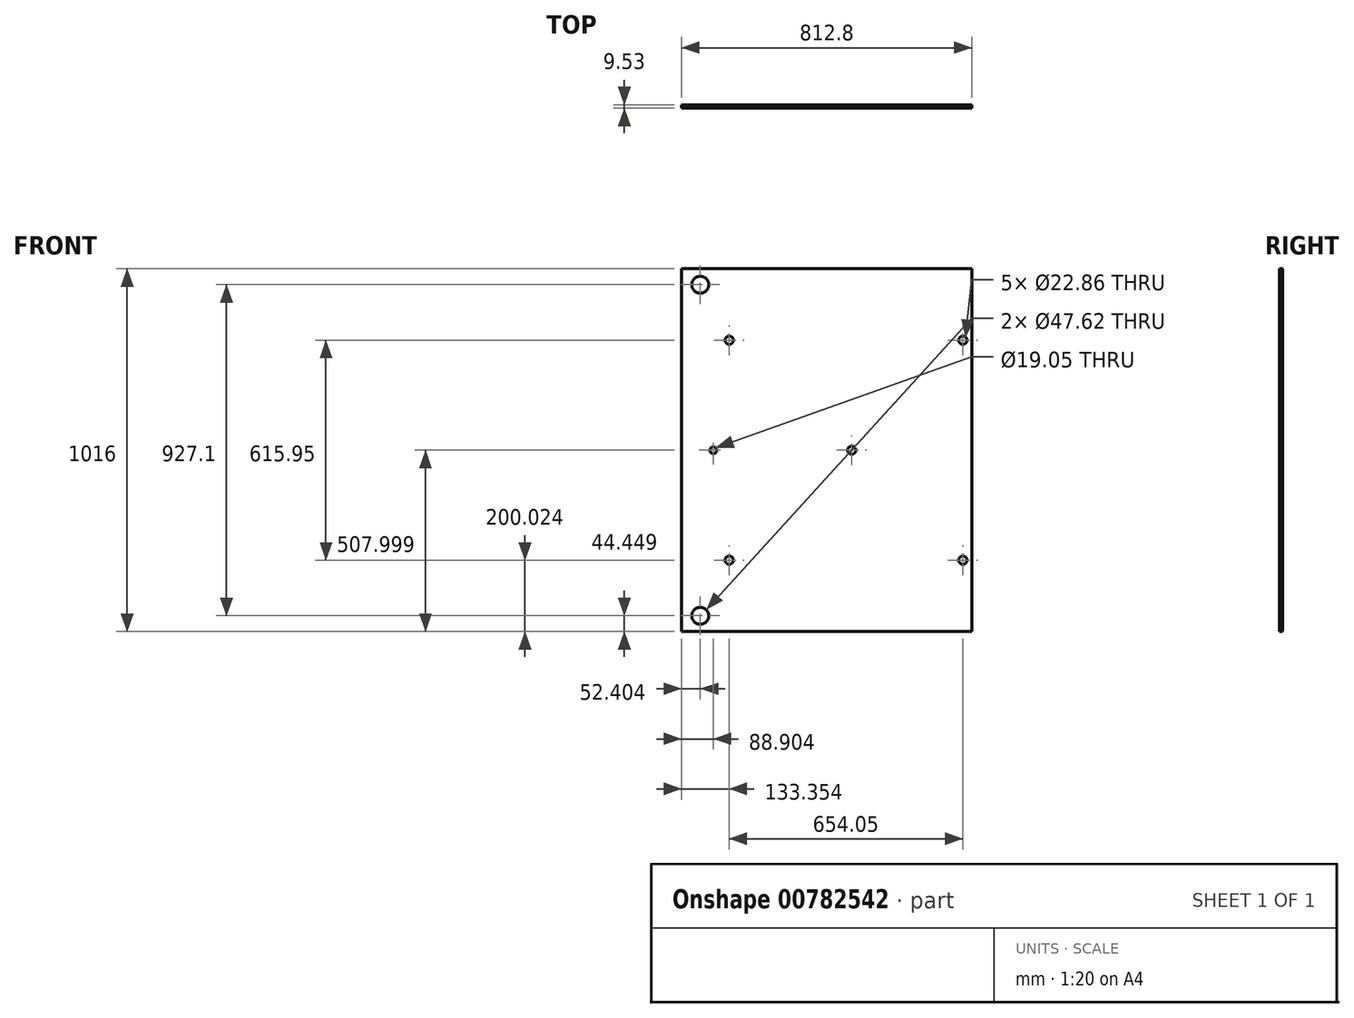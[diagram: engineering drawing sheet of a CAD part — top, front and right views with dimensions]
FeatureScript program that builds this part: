
annotation { "Feature Type Name" : "Feature", "Feature Type Description" : "" }
export const myFeature = defineFeature(function(context is Context, id is Id, definition is map)
    precondition{}
    {
        {
            var Q0;
            Q0=qCreatedBy(makeId("Front.planeOp"),FACE);
            var sketch = newSketch(context, id + "F0", { "sketchPlane" : qUnion([Q0])});
            skLineSegment(sketch, "E0.bottom", {"start": v(-774.87, 984.8) * mm, "end": v(37.93, 984.8) * mm});
            skLineSegment(sketch, "E0.top", {"start": v(-774.87, -31.2) * mm, "end": v(37.93, -31.2) * mm});
            skLineSegment(sketch, "E0.left", {"start": v(-774.87, 984.8) * mm, "end": v(-774.87, -31.2) * mm});
            skLineSegment(sketch, "E0.right", {"start": v(37.93, 984.8) * mm, "end": v(37.93, -31.2) * mm});
            skSolve(sketch);
        }
        {
            var Q0;
            Q0 = qSketchRegion(id + "F0", true);
            extrude(context, id + "F1", {"entities" : qUnion([Q0]), "depth" : 9.52 * mm, "offsetDistance" : 25.4 * mm});
        }
        {
            var Q0;
            Q0=qCreatedBy(makeId("Front.planeOp"),FACE);
            var sketch = newSketch(context, id + "F2", { "sketchPlane" : qUnion([Q0])});
            skPoint(sketch, "E1", {"position": v(-641.52, 784.77) * mm});
            skPoint(sketch, "E2", {"position": v(-641.52, 168.82) * mm});
            skPoint(sketch, "E3", {"position": v(-685.97, 476.8) * mm});
            skPoint(sketch, "E4", {"position": v(-298.62, 476.8) * mm});
            skPoint(sketch, "E5", {"position": v(12.53, 784.77) * mm});
            skPoint(sketch, "E6", {"position": v(12.53, 168.82) * mm});
            skPoint(sketch, "E7", {"position": v(-722.47, 940.35) * mm});
            skPoint(sketch, "E8", {"position": v(-722.47, 13.25) * mm});
            skSolve(sketch);
        }
        {
            var Q0;
            Q0=sQuery(id+"F2.wireOp",VERTEX,"E7");
            var Q1;
            Q1=sQuery(id+"F2.wireOp",VERTEX,"E8");
            var Q2;
            Q2=makeQuery(id+"F1.opExtrude","SWEPT_BODY",BODY,{"disambiguationData":[OSD([sQuery(id+"F0.wireOp",EDGE,"E0.bottom"),sQuery(id+"F0.wireOp",EDGE,"E0.top"),sQuery(id+"F0.wireOp",EDGE,"E0.left"),sQuery(id+"F0.wireOp",EDGE,"E0.right")])]});
            hole(context, id + "F3", {"style" : HoleStyle.SIMPLE, "endStyle" : HoleEndStyle.THROUGH, "oppositeDirection" : true, "holeDiameter" : 47.62 * mm, "majorDiameter" : 6.35 * mm, "isTappedThrough" : true, "tappedDepth" : 12.7 * mm, "tapClearance" : 3, "locations" : qUnion([Q0, Q1]), "scope" : qUnion([Q2]), "startStyle" : HoleStartStyle.PART});
        }
        {
            var Q0;
            Q0=sQuery(id+"F2.wireOp",VERTEX,"E3");
            var Q1;
            Q1=makeQuery(id+"F1.opExtrude","SWEPT_BODY",BODY,{"disambiguationData":[OSD([sQuery(id+"F0.wireOp",EDGE,"E0.bottom"),sQuery(id+"F0.wireOp",EDGE,"E0.top"),sQuery(id+"F0.wireOp",EDGE,"E0.left"),sQuery(id+"F0.wireOp",EDGE,"E0.right")])]});
            hole(context, id + "F4", {"style" : HoleStyle.SIMPLE, "endStyle" : HoleEndStyle.THROUGH, "oppositeDirection" : true, "holeDiameter" : 19.05 * mm, "majorDiameter" : 6.35 * mm, "isTappedThrough" : true, "tappedDepth" : 12.7 * mm, "tapClearance" : 3, "locations" : qUnion([Q0]), "scope" : qUnion([Q1]), "startStyle" : HoleStartStyle.PART});
        }
        {
            var Q0;
            Q0=sQuery(id+"F2.wireOp",VERTEX,"E1");
            var Q1;
            Q1=sQuery(id+"F2.wireOp",VERTEX,"E4");
            var Q2;
            Q2=sQuery(id+"F2.wireOp",VERTEX,"E5");
            var Q3;
            Q3=sQuery(id+"F2.wireOp",VERTEX,"E6");
            var Q4;
            Q4=sQuery(id+"F2.wireOp",VERTEX,"E2");
            var Q5;
            Q5=makeQuery(id+"F1.opExtrude","SWEPT_BODY",BODY,{"disambiguationData":[OSD([sQuery(id+"F0.wireOp",EDGE,"E0.bottom"),sQuery(id+"F0.wireOp",EDGE,"E0.top"),sQuery(id+"F0.wireOp",EDGE,"E0.left"),sQuery(id+"F0.wireOp",EDGE,"E0.right")])]});
            hole(context, id + "F5", {"style" : HoleStyle.SIMPLE, "endStyle" : HoleEndStyle.THROUGH, "oppositeDirection" : true, "holeDiameter" : 22.86 * mm, "majorDiameter" : 6.35 * mm, "isTappedThrough" : true, "tappedDepth" : 12.7 * mm, "tapClearance" : 3, "locations" : qUnion([Q0, Q1, Q2, Q3, Q4]), "scope" : qUnion([Q5]), "startStyle" : HoleStartStyle.PART});
        }
    });
